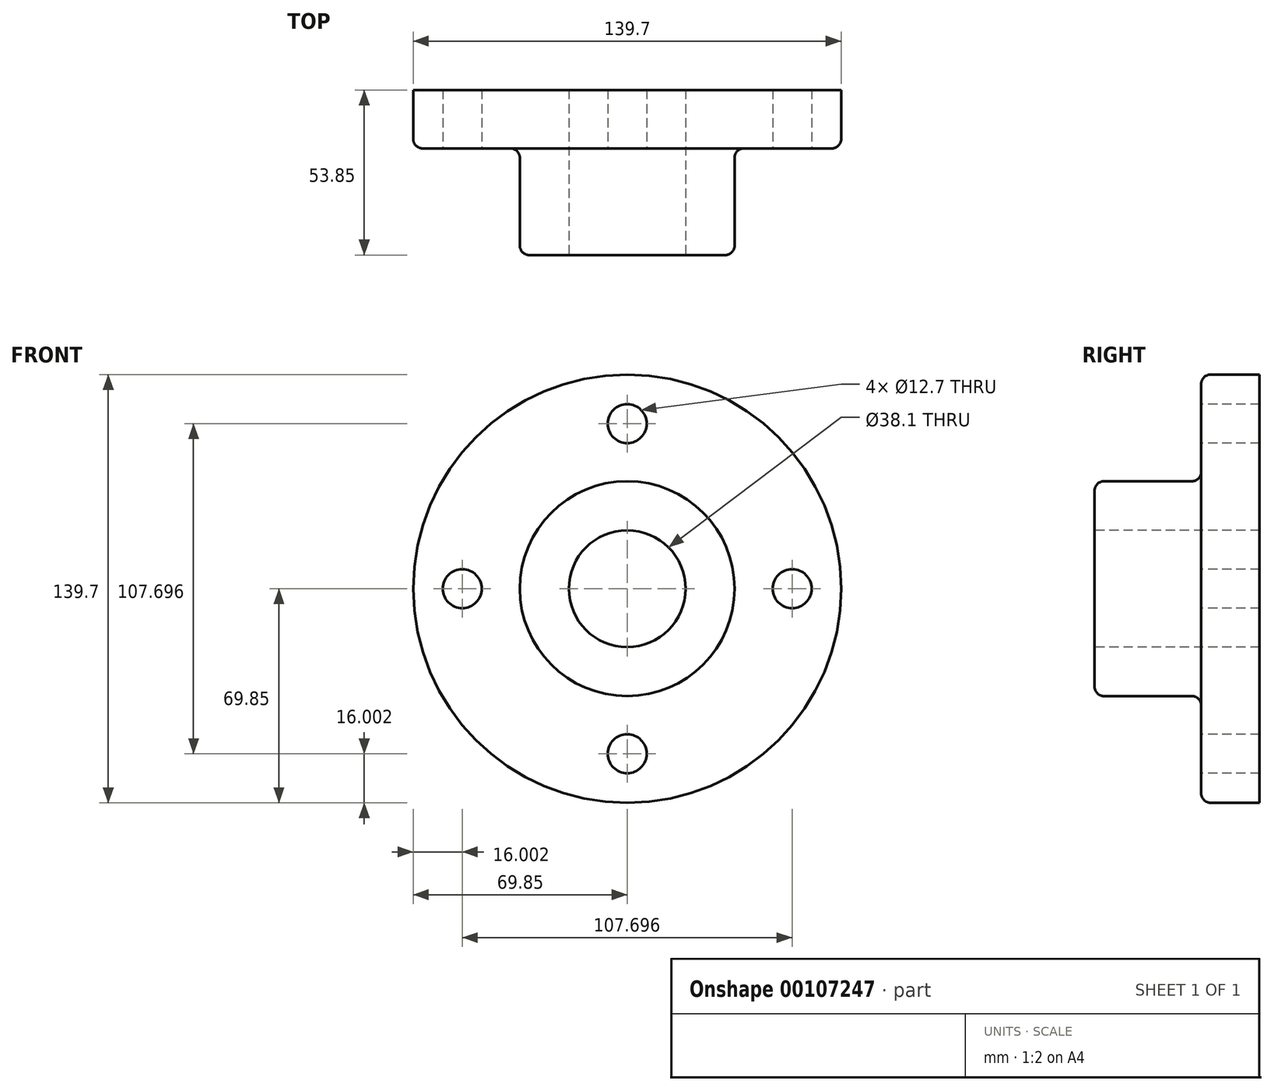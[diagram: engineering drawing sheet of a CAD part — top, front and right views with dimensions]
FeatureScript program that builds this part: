
annotation { "Feature Type Name" : "Feature", "Feature Type Description" : "" }
export const myFeature = defineFeature(function(context is Context, id is Id, definition is map)
    precondition{}
    {
        {
            var Q0;
            Q0=qCreatedBy(makeId("Right.planeOp"),FACE);
            var sketch = newSketch(context, id + "F0", { "sketchPlane" : qUnion([Q0])});
            skLineSegment(sketch, "E0", {"start": v(-88.44, 0) * mm, "end": v(91.08, 0) * mm, "construction": true});
            skLineSegment(sketch, "E1", {"start": v(-53.85, 19.05) * mm, "end": v(-53.85, 35.05) * mm});
            skLineSegment(sketch, "E2", {"start": v(-53.85, 35.05) * mm, "end": v(-19.05, 35.05) * mm});
            skLineSegment(sketch, "E3", {"start": v(-19.05, 35.05) * mm, "end": v(-19.05, 69.85) * mm});
            skLineSegment(sketch, "E4", {"start": v(-19.05, 69.85) * mm, "end": v(0, 69.85) * mm});
            skLineSegment(sketch, "E5", {"start": v(0, 69.85) * mm, "end": v(0, 19.05) * mm});
            skLineSegment(sketch, "E6", {"start": v(0, 19.05) * mm, "end": v(-53.85, 19.05) * mm});
            skSolve(sketch);
        }
        {
            var Q0;
            Q0 = qSketchRegion(id + "F0", true);
            var Q1;
            Q1=sQuery(id+"F0.wireOp",EDGE,"E0");
            revolve(context, id + "F1", {"entities" : qUnion([Q0]), "axis" : qUnion([Q1]), "revolveType" : RevolveType.FULL});
        }
        {
            var Q0;
            Q0=makeQuery(id+"F1.opRevolve","SWEPT_EDGE",EDGE,{"disambiguationData":[OSD([sQuery(id+"F0.wireOp",EDGE,"E3"),sQuery(id+"F0.wireOp",EDGE,"E4")])]});
            var Q1;
            Q1=makeQuery(id+"F1.opRevolve","SWEPT_EDGE",EDGE,{"disambiguationData":[OSD([sQuery(id+"F0.wireOp",EDGE,"E1"),sQuery(id+"F0.wireOp",EDGE,"E2")])]});
            var Q2;
            Q2=makeQuery(id+"F1.opRevolve","SWEPT_EDGE",EDGE,{"disambiguationData":[OSD([sQuery(id+"F0.wireOp",EDGE,"E2"),sQuery(id+"F0.wireOp",EDGE,"E3")])]});
            fillet(context, id + "F2", {"entities" : qUnion([Q0, Q1, Q2]), "radius" : 3.05 * mm, "tangentPropagation" : true, "allowEdgeOverflow" : false});
        }
        {
            var Q0;
            Q0=makeQuery(id+"F1.opRevolve","SWEPT_FACE",FACE,{"disambiguationData":[OSD([sQuery(id+"F0.wireOp",EDGE,"E3")])]});
            var sketch = newSketch(context, id + "F3", { "sketchPlane" : qUnion([Q0])});
            skCircle(sketch, "E7", {"center": v(0, 0) * mm, "radius": 53.85 * mm, "construction": true});
            skCircle(sketch, "E8", {"center": v(0, 53.85) * mm, "radius": 6.35 * mm});
            skCircle(sketch, "E9", {"center": v(53.85, 0) * mm, "radius": 6.35 * mm});
            skCircle(sketch, "E10", {"center": v(0, -53.85) * mm, "radius": 6.35 * mm});
            skCircle(sketch, "E11", {"center": v(-53.85, 0) * mm, "radius": 6.35 * mm});
            skSolve(sketch);
        }
        {
            var Q0;
            Q0 = qSketchRegion(id + "F3", true);
            extrude(context, id + "F4", {"entities" : qUnion([Q0]), "operationType" : NewBodyOperationType.REMOVE, "endBound" : BoundingType.THROUGH_ALL, "oppositeDirection" : true, "depth" : 25.4 * mm});
        }
    });
